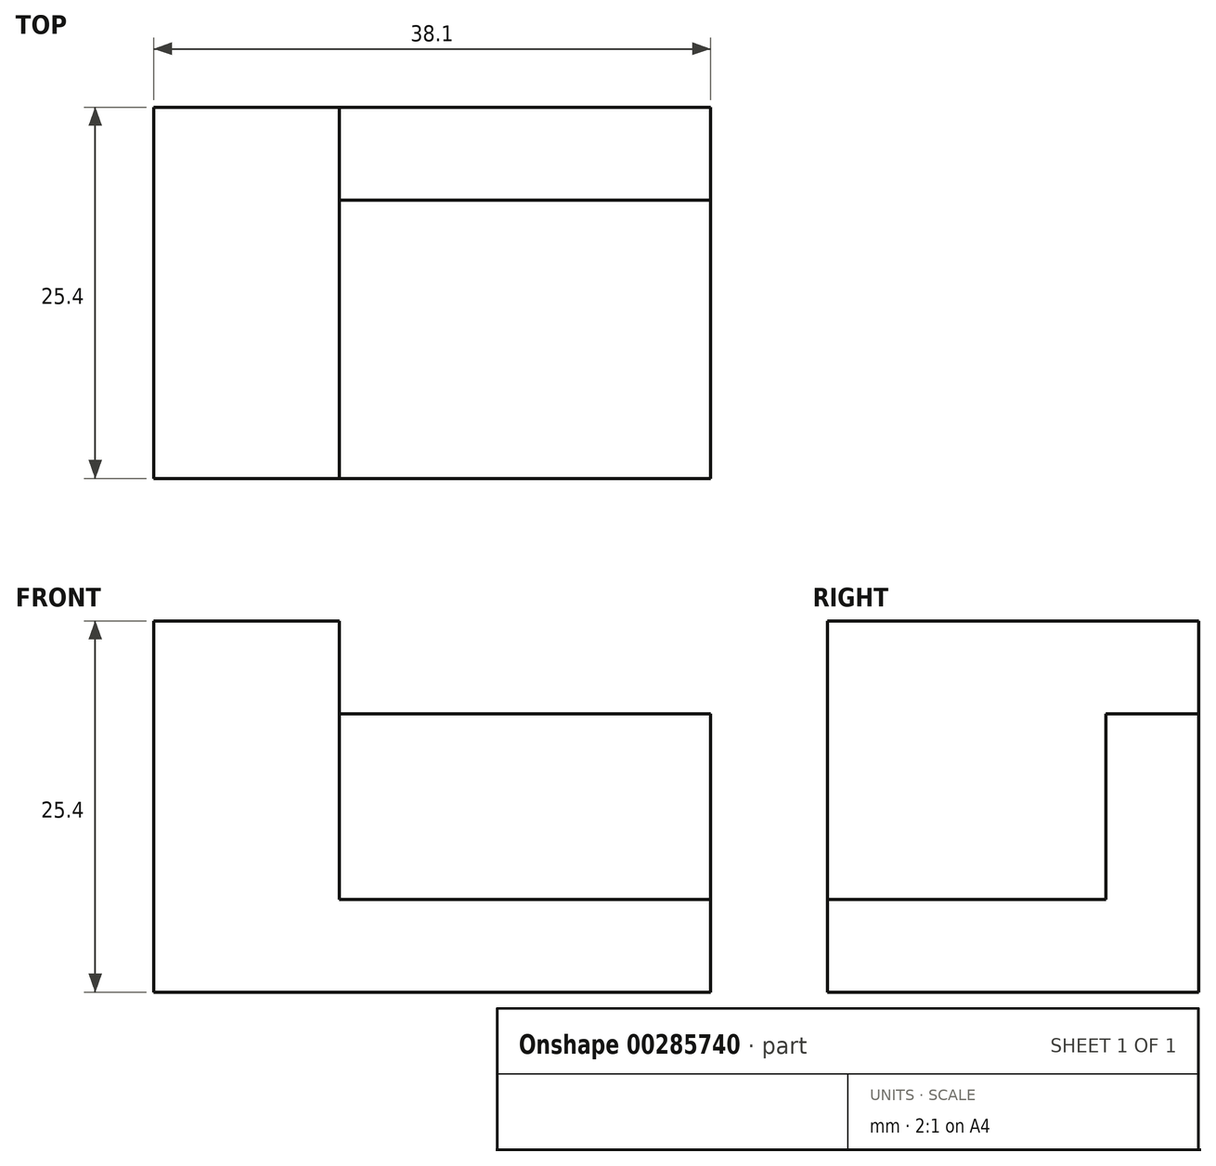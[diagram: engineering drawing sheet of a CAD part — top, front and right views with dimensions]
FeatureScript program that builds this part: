
annotation { "Feature Type Name" : "Feature", "Feature Type Description" : "" }
export const myFeature = defineFeature(function(context is Context, id is Id, definition is map)
    precondition{}
    {
        {
            var Q0;
            Q0=qCreatedBy(makeId("Front.planeOp"),FACE);
            var sketch = newSketch(context, id + "F0", { "sketchPlane" : qUnion([Q0])});
            skLineSegment(sketch, "E0", {"start": v(0, 0) * mm, "end": v(0, 25.4) * mm});
            skLineSegment(sketch, "E1", {"start": v(0, 25.4) * mm, "end": v(12.7, 25.4) * mm});
            skLineSegment(sketch, "E2", {"start": v(12.7, 25.4) * mm, "end": v(12.7, 6.35) * mm});
            skLineSegment(sketch, "E3", {"start": v(12.7, 6.35) * mm, "end": v(38.1, 6.35) * mm});
            skLineSegment(sketch, "E4", {"start": v(38.1, 6.35) * mm, "end": v(38.1, 0) * mm});
            skLineSegment(sketch, "E5", {"start": v(38.1, 0) * mm, "end": v(0, 0) * mm});
            skSolve(sketch);
        }
        {
            var Q0;
            Q0 = qSketchRegion(id + "F0", true);
            extrude(context, id + "F1", {"entities" : qUnion([Q0]), "depth" : 25.4 * mm});
        }
        {
            var Q0;
            Q0=makeQuery(id+"F1.opExtrude","SWEPT_FACE",FACE,{"disambiguationData":[OSD([sQuery(id+"F0.wireOp",EDGE,"E4")])]});
            var sketch = newSketch(context, id + "F2", { "sketchPlane" : qUnion([Q0])});
            skLineSegment(sketch, "E6", {"start": v(0, 6.35) * mm, "end": v(0, 19.05) * mm});
            skLineSegment(sketch, "E7", {"start": v(0, 19.05) * mm, "end": v(-6.35, 19.05) * mm});
            skLineSegment(sketch, "E8", {"start": v(-6.35, 19.05) * mm, "end": v(-6.35, 6.35) * mm});
            skLineSegment(sketch, "E9", {"start": v(0, 6.35) * mm, "end": v(-6.35, 6.35) * mm});
            skSolve(sketch);
        }
        {
            var Q0;
            Q0 = qSketchRegion(id + "F2", true);
            extrude(context, id + "F3", {"entities" : qUnion([Q0]), "operationType" : NewBodyOperationType.ADD, "oppositeDirection" : true, "depth" : 25.4 * mm});
        }
    });
